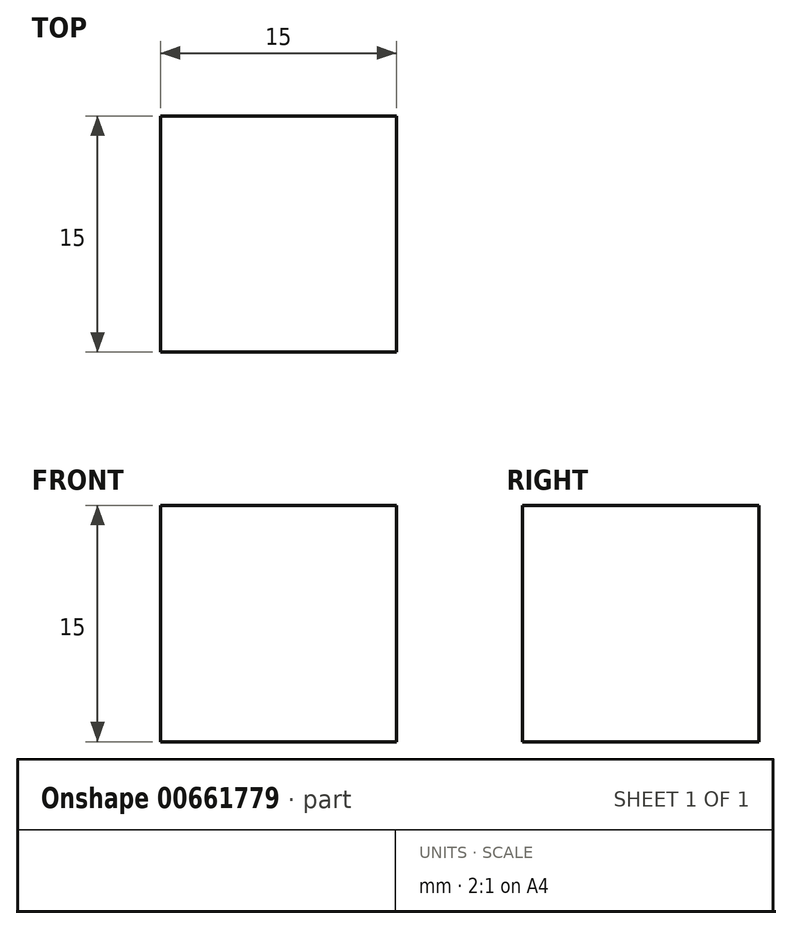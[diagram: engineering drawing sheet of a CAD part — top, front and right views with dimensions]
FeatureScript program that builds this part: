
annotation { "Feature Type Name" : "Feature", "Feature Type Description" : "" }
export const myFeature = defineFeature(function(context is Context, id is Id, definition is map)
    precondition{}
    {
        {
            var Q0;
            Q0=qCreatedBy(makeId("Top.planeOp"),FACE);
            var sketch = newSketch(context, id + "F0", { "sketchPlane" : qUnion([Q0])});
            skLineSegment(sketch, "E0.bottom", {"start": v(7.5, -7.5) * mm, "end": v(-7.5, -7.5) * mm});
            skLineSegment(sketch, "E0.top", {"start": v(7.5, 7.5) * mm, "end": v(-7.5, 7.5) * mm});
            skLineSegment(sketch, "E0.left", {"start": v(7.5, -7.5) * mm, "end": v(7.5, 7.5) * mm});
            skLineSegment(sketch, "E0.right", {"start": v(-7.5, -7.5) * mm, "end": v(-7.5, 7.5) * mm});
            skPoint(sketch, "E0.middle", {"position": v(0, 0) * mm});
            skSolve(sketch);
        }
        {
            var Q0;
            Q0=makeQuery(id+"F0.imprint","IMPRINT",FACE,{"disambiguationData":[TD([[makeQuery(id+"F0.imprint","IMPRINT",EDGE,{"derivedFrom":sQuery(id+"F0.wireOp",EDGE,"E0.bottom")}),-1.0]])]});
            extrude(context, id + "F1", {"entities" : qUnion([Q0]), "depth" : 15 * mm, "offsetDistance" : 25 * mm});
        }
    });
